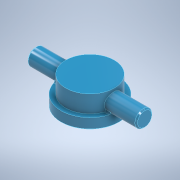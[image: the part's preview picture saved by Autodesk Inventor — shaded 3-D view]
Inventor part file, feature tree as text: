
AUTODESK INVENTOR PART (.ipt)
format: ipt  version: 2021 (Build 250183000, 183)  size: 163,840 bytes
history: native  units: mm
features: sketch x3, extrude x2, chamfer x2, revolve x1, fillet x1
ambient origin geometry x8: Origin, YZ Plane, XZ Plane, XY Plane, X Axis, Y Axis, Z Axis, Center Point
bodies: Solid1 (feature_tree)
feature tree (9):
  extrude  "Extrusion1"  Depth=3.9mm TaperAngle=0.0deg
  extrude  "Extrusion2"  Depth=6.55mm TaperAngle=0.0deg
  revolve  "Revolution1"  [1 undecoded]
  chamfer  "Chamfer1"  Distance=3.2mm
  fillet  "Fillet1"  [1 undecoded]
  chamfer  "Chamfer2"  Distance=0.5mm Angle=45.0deg
  sketch  "Sketch1"  dims[d0=22.0mm d1=3.9mm d2=0.0mm]
  sketch  "Sketch2"  dims[d3=18.4mm d4=6.55mm d5=0.0mm]
  sketch  "Sketch3"  dims[d6=6.1mm d7=41.5mm d8=3.2mm d9=360.0deg d10=0.5mm d11=2.0mm d12=45.0deg d13=0.5mm d14=0.2mm d15=2.0mm d16=45.0deg]
note: 2 required parameter values undecoded (feature->parameter linkage not recoverable at this tier; creation-order binding heuristic only, values carry confidence <= 0.55)